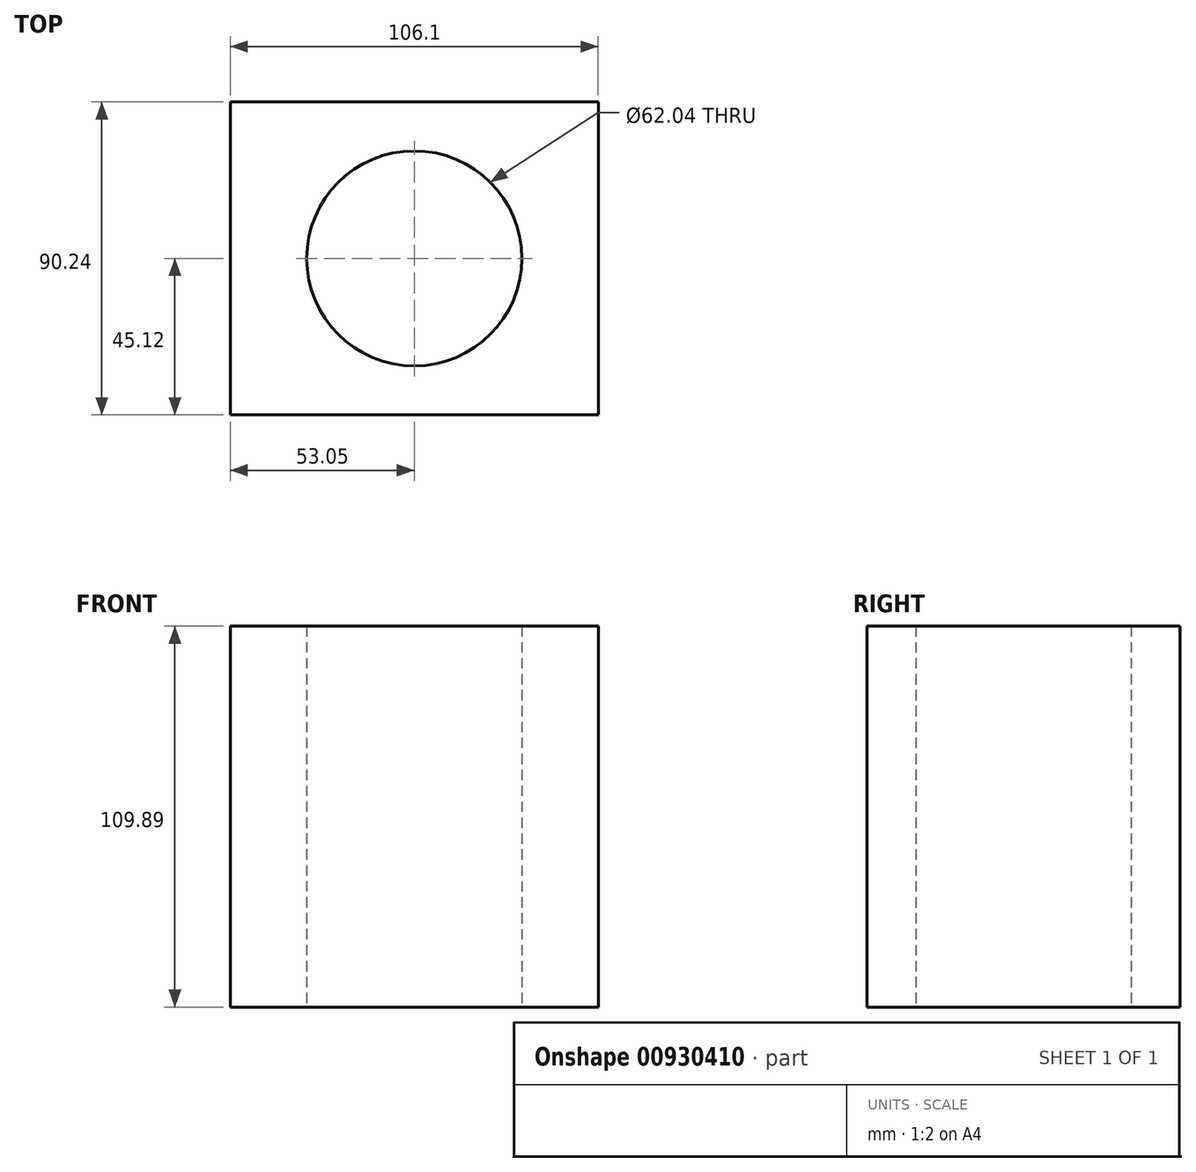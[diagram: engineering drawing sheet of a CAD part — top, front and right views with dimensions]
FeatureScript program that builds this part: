
annotation { "Feature Type Name" : "Feature", "Feature Type Description" : "" }
export const myFeature = defineFeature(function(context is Context, id is Id, definition is map)
    precondition{}
    {
        {
            var Q0;
            Q0=qCreatedBy(makeId("Top.planeOp"),FACE);
            var sketch = newSketch(context, id + "F0", { "sketchPlane" : qUnion([Q0])});
            skLineSegment(sketch, "E0.bottom", {"start": v(53.05, 45.12) * mm, "end": v(-53.05, 45.12) * mm});
            skLineSegment(sketch, "E0.top", {"start": v(53.05, -45.12) * mm, "end": v(-53.05, -45.12) * mm});
            skLineSegment(sketch, "E0.left", {"start": v(53.05, 45.12) * mm, "end": v(53.05, -45.12) * mm});
            skLineSegment(sketch, "E0.right", {"start": v(-53.05, 45.12) * mm, "end": v(-53.05, -45.12) * mm});
            skPoint(sketch, "E0.middle", {"position": v(0, 0) * mm});
            skCircle(sketch, "E1", {"center": v(0, 0) * mm, "radius": 31.02 * mm});
            skSolve(sketch);
        }
        {
            var Q0;
            Q0=makeQuery(id+"F0.imprint","IMPRINT",FACE,{"disambiguationData":[TD([[makeQuery(id+"F0.imprint","IMPRINT",EDGE,{"derivedFrom":sQuery(id+"F0.wireOp",EDGE,"E1")}),1.0]])]});
            var sketch = newSketch(context, id + "F1", { "sketchPlane" : qUnion([Q0])});
            skSolve(sketch);
        }
        {
            var Q0;
            Q0=makeQuery(id+"F1.imprint","IMPRINT",FACE,{"disambiguationData":[TD([[makeQuery(id+"F1.imprint","IMPRINT",EDGE,{"derivedFrom":makeQuery(id+"F0.imprint","IMPRINT",EDGE,{"derivedFrom":sQuery(id+"F0.wireOp",EDGE,"E1")})}),1.0]])]});
            var Q1;
            Q1=makeQuery(id+"F0.imprint","IMPRINT",FACE,{"disambiguationData":[TD([[makeQuery(id+"F0.imprint","IMPRINT",EDGE,{"derivedFrom":sQuery(id+"F0.wireOp",EDGE,"E0.bottom")}),1.0]])]});
            extrude(context, id + "F2", {"entities" : qUnion([Q0, Q1]), "depth" : 109.9 * mm, "offsetDistance" : 25.4 * mm});
        }
    });
